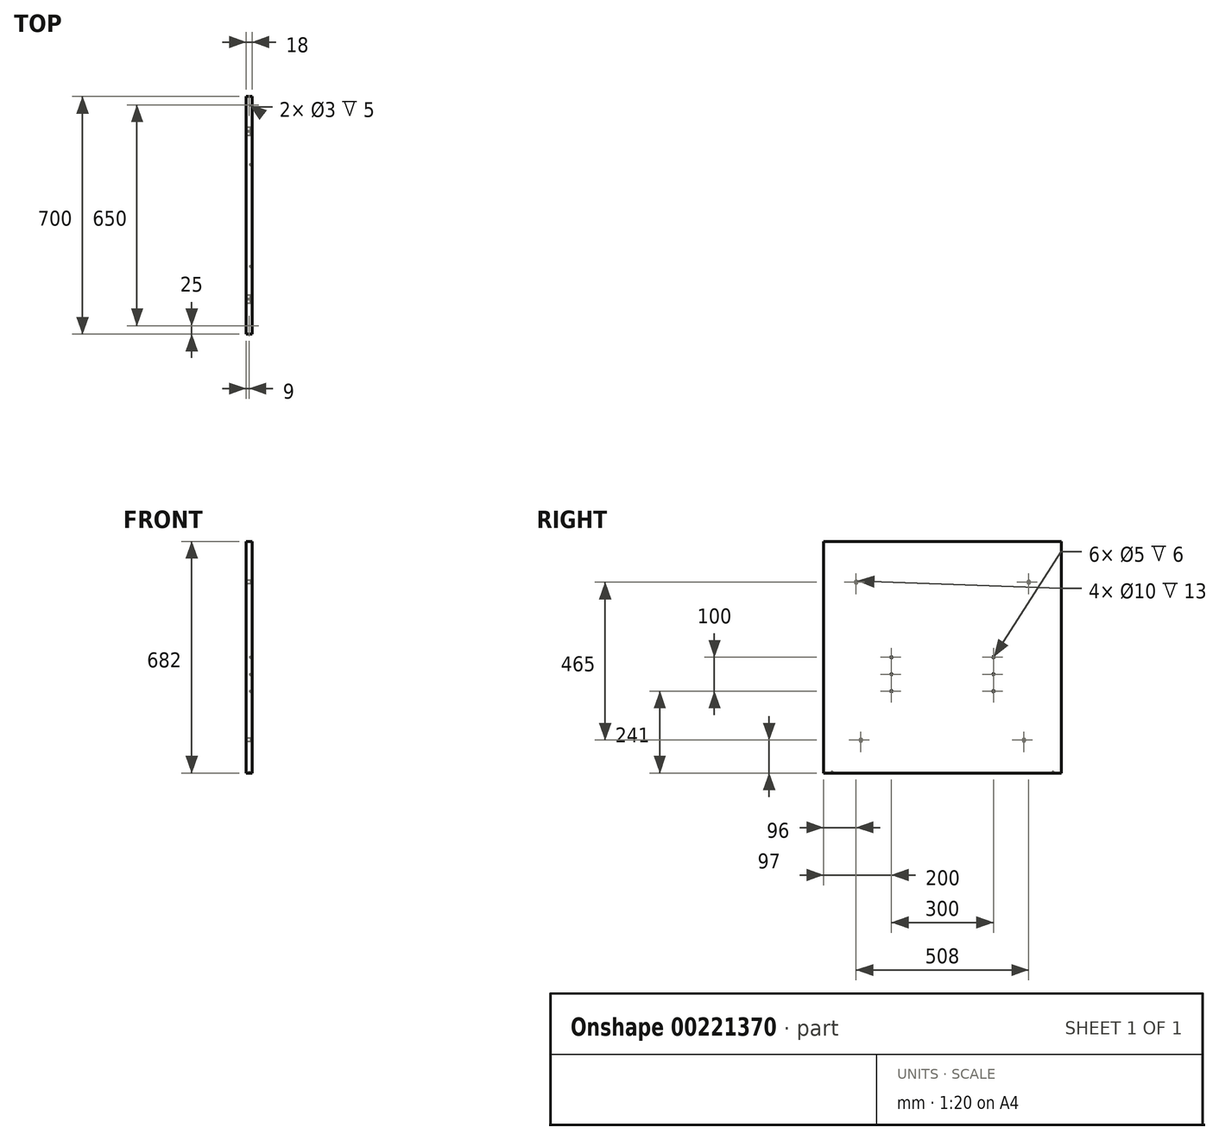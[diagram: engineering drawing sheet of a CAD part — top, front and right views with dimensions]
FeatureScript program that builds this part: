
annotation { "Feature Type Name" : "Feature", "Feature Type Description" : "" }
export const myFeature = defineFeature(function(context is Context, id is Id, definition is map)
    precondition{}
    {
        {
            var Q0;
            Q0=qCreatedBy(makeId("Right.planeOp"),FACE);
            var sketch = newSketch(context, id + "F0", { "sketchPlane" : qUnion([Q0])});
            skLineSegment(sketch, "E0.bottom", {"start": v(350, -341) * mm, "end": v(-350, -341) * mm});
            skLineSegment(sketch, "E0.top", {"start": v(350, 341) * mm, "end": v(-350, 341) * mm});
            skLineSegment(sketch, "E0.left", {"start": v(350, -341) * mm, "end": v(350, 341) * mm});
            skLineSegment(sketch, "E0.right", {"start": v(-350, -341) * mm, "end": v(-350, 341) * mm});
            skPoint(sketch, "E0.middle", {"position": v(0, 0) * mm});
            skSolve(sketch);
        }
        {
            var Q0;
            Q0=qSketchRegion(id+"F0",true);
            extrude(context, id + "F1", {"entities" : qUnion([Q0]), "depth" : 18 * mm});
        }
        {
            var Q0;
            Q0=makeQuery(id+"F1.opExtrude","SWEPT_FACE",FACE,{"disambiguationData":[OSD([sQuery(id+"F0.wireOp",EDGE,"E0.bottom")])]});
            var sketch = newSketch(context, id + "F2", { "sketchPlane" : qUnion([Q0])});
            skCircle(sketch, "E1", {"center": v(9, 325) * mm, "radius": 1.5 * mm});
            skCircle(sketch, "E2", {"center": v(9, -325) * mm, "radius": 1.5 * mm});
            skSolve(sketch);
        }
        {
            var Q0;
            Q0=qSketchRegion(id+"F2",true);
            extrude(context, id + "F3", {"entities" : qUnion([Q0]), "operationType" : NewBodyOperationType.REMOVE, "oppositeDirection" : true, "depth" : 5 * mm});
        }
        {
            var Q0;
            Q0=makeQuery(id+"F1.opExtrude","CAP_FACE",FACE,{"disambiguationData":[OSD([sQuery(id+"F0.wireOp",EDGE,"E0.bottom"),sQuery(id+"F0.wireOp",EDGE,"E0.top"),sQuery(id+"F0.wireOp",EDGE,"E0.left"),sQuery(id+"F0.wireOp",EDGE,"E0.right")])],"isStart":true});
            var sketch = newSketch(context, id + "F4", { "sketchPlane" : qUnion([Q0])});
            skCircle(sketch, "E3", {"center": v(-254, 221) * mm, "radius": 5 * mm});
            skCircle(sketch, "E4", {"center": v(254, 221) * mm, "radius": 5 * mm});
            skCircle(sketch, "E5", {"center": v(-240, -244) * mm, "radius": 5 * mm});
            skCircle(sketch, "E6", {"center": v(240, -244) * mm, "radius": 5 * mm});
            skSolve(sketch);
        }
        {
            var Q0;
            Q0 = qSketchRegion(id + "F4", true);
            extrude(context, id + "F5", {"entities" : qUnion([Q0]), "operationType" : NewBodyOperationType.REMOVE, "oppositeDirection" : true, "depth" : 13 * mm});
        }
        {
            var Q0;
            Q0=makeQuery(id+"F1.opExtrude","CAP_FACE",FACE,{"disambiguationData":[OSD([sQuery(id+"F0.wireOp",EDGE,"E0.bottom"),sQuery(id+"F0.wireOp",EDGE,"E0.top"),sQuery(id+"F0.wireOp",EDGE,"E0.left"),sQuery(id+"F0.wireOp",EDGE,"E0.right")])],"isStart":false});
            var sketch = newSketch(context, id + "F6", { "sketchPlane" : qUnion([Q0])});
            skCircle(sketch, "E7", {"center": v(-150, 0) * mm, "radius": 2.5 * mm});
            skCircle(sketch, "E8", {"center": v(150, 0) * mm, "radius": 2.5 * mm});
            skCircle(sketch, "E9.0.1.0", {"center": v(-150, -50) * mm, "radius": 2.5 * mm});
            skCircle(sketch, "E9.0.1.1", {"center": v(150, -50) * mm, "radius": 2.5 * mm});
            skCircle(sketch, "E9.0.2.0", {"center": v(-150, -100) * mm, "radius": 2.5 * mm});
            skCircle(sketch, "E9.0.2.1", {"center": v(150, -100) * mm, "radius": 2.5 * mm});
            skLineSegment(sketch, "E9.direction1", {"start": v(-150, 0) * mm, "end": v(-125, 0) * mm, "construction": true});
            skLineSegment(sketch, "E9.direction2", {"start": v(-150, 0) * mm, "end": v(-150, -50) * mm, "construction": true});
            skSolve(sketch);
        }
        {
            var Q0;
            Q0 = qSketchRegion(id + "F6", true);
            extrude(context, id + "F7", {"entities" : qUnion([Q0]), "operationType" : NewBodyOperationType.REMOVE, "oppositeDirection" : true, "depth" : 6 * mm});
        }
    });
